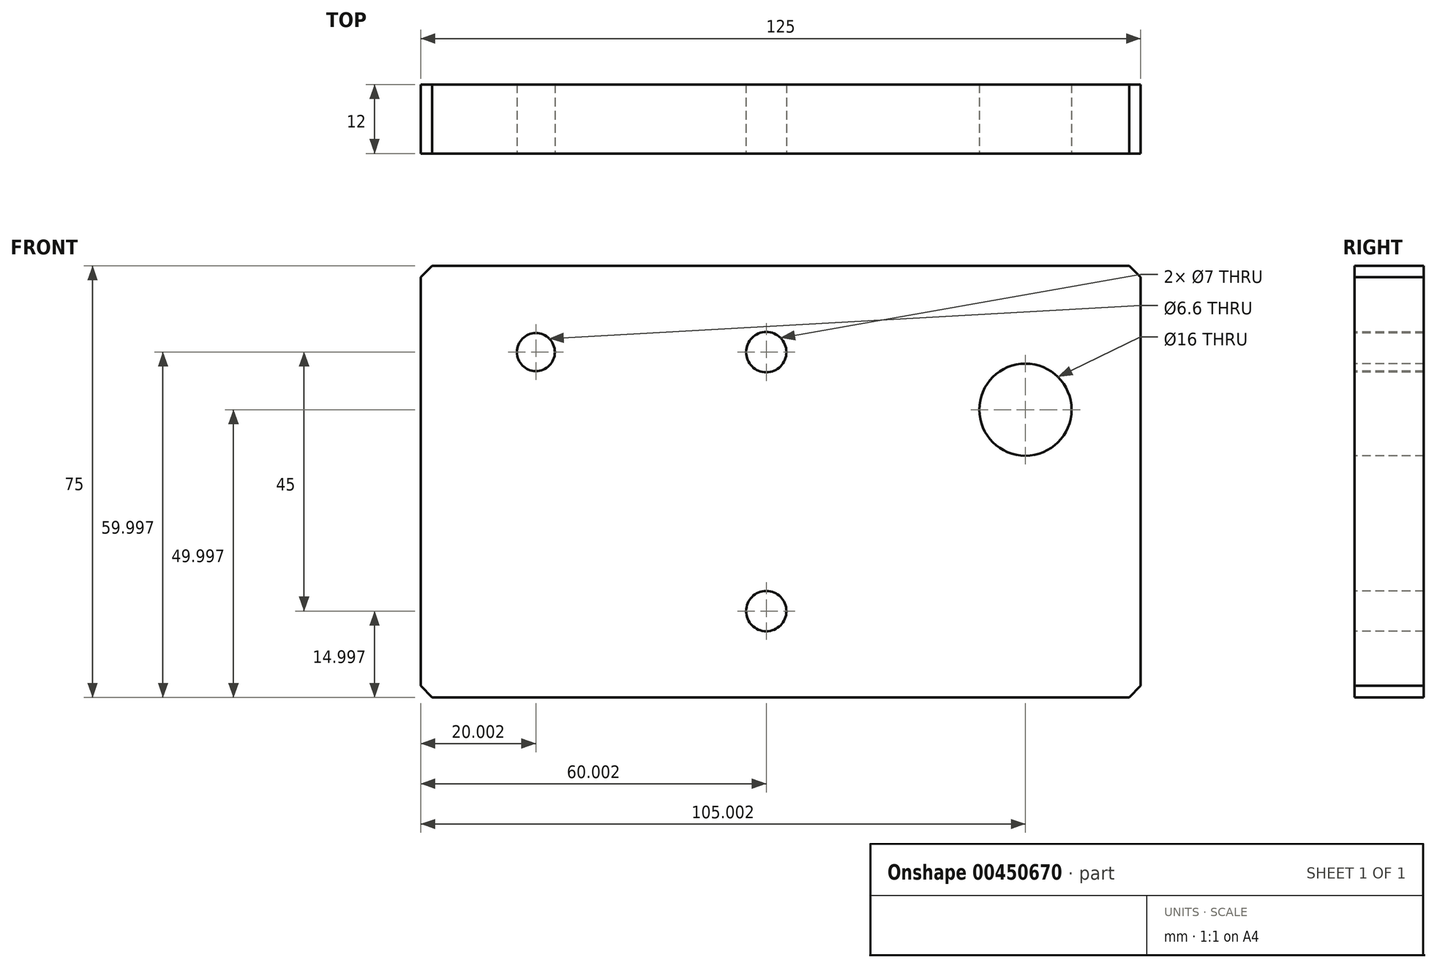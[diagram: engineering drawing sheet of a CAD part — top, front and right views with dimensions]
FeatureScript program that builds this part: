
annotation { "Feature Type Name" : "Feature", "Feature Type Description" : "" }
export const myFeature = defineFeature(function(context is Context, id is Id, definition is map)
    precondition{}
    {
        {
            var Q0;
            Q0=qCreatedBy(makeId("Front.planeOp"),FACE);
            var sketch = newSketch(context, id + "F0", { "sketchPlane" : qUnion([Q0])});
            skLineSegment(sketch, "E0", {"start": v(56.37, -134.41) * mm, "end": v(44.37, -134.41) * mm});
            skLineSegment(sketch, "E1", {"start": v(56.37, -59.41) * mm, "end": v(44.37, -59.41) * mm});
            skLineSegment(sketch, "E2", {"start": v(56.37, -59.41) * mm, "end": v(56.37, -134.41) * mm});
            skLineSegment(sketch, "E3", {"start": v(44.37, -59.41) * mm, "end": v(44.37, -134.41) * mm});
            skLineSegment(sketch, "E4", {"start": v(-19.08, -134.41) * mm, "end": v(-140.08, -134.41) * mm});
            skLineSegment(sketch, "E5", {"start": v(-17.08, -132.41) * mm, "end": v(-19.08, -134.41) * mm});
            skLineSegment(sketch, "E6", {"start": v(-19.08, -59.41) * mm, "end": v(-140.08, -59.41) * mm});
            skLineSegment(sketch, "E7", {"start": v(-17.08, -61.41) * mm, "end": v(-19.08, -59.41) * mm});
            skLineSegment(sketch, "E8", {"start": v(-17.08, -61.41) * mm, "end": v(-17.08, -132.41) * mm});
            skLineSegment(sketch, "E9", {"start": v(-142.08, -61.41) * mm, "end": v(-142.08, -132.41) * mm});
            skLineSegment(sketch, "E10", {"start": v(-140.08, -59.41) * mm, "end": v(-142.08, -61.41) * mm});
            skLineSegment(sketch, "E11", {"start": v(-140.08, -134.41) * mm, "end": v(-142.08, -132.41) * mm});
            skLineSegment(sketch, "E12", {"start": v(-37.08, -74.04) * mm, "end": v(-37.08, -94.79) * mm});
            skLineSegment(sketch, "E13", {"start": v(-47.45, -84.41) * mm, "end": v(-26.7, -84.41) * mm});
            skCircle(sketch, "E14", {"center": v(-37.08, -84.41) * mm, "radius": 8 * mm});
            skCircle(sketch, "E15", {"center": v(-37.08, -84.41) * mm, "radius": 6.92 * mm});
            skCircle(sketch, "E16", {"center": v(-82.08, -74.41) * mm, "radius": 3.5 * mm});
            skLineSegment(sketch, "E17", {"start": v(-82.08, -69.86) * mm, "end": v(-82.08, -78.96) * mm});
            skLineSegment(sketch, "E18", {"start": v(-86.63, -74.41) * mm, "end": v(-77.53, -74.41) * mm});
            skLineSegment(sketch, "E19", {"start": v(-122.08, -69.86) * mm, "end": v(-122.08, -78.96) * mm});
            skLineSegment(sketch, "E20", {"start": v(-126.63, -74.41) * mm, "end": v(-117.53, -74.41) * mm});
            skCircle(sketch, "E21", {"center": v(-82.08, -119.41) * mm, "radius": 3.5 * mm});
            skLineSegment(sketch, "E22", {"start": v(-82.08, -114.86) * mm, "end": v(-82.08, -123.96) * mm});
            skLineSegment(sketch, "E23", {"start": v(-86.63, -119.41) * mm, "end": v(-77.53, -119.41) * mm});
            skCircle(sketch, "E24", {"center": v(-122.08, -74.41) * mm, "radius": 3.3 * mm});
            skSolve(sketch);
        }
        {
            var Q0;
            Q0=makeQuery(id+"F0.imprint","IMPRINT",FACE,{"disambiguationData":[TD([[makeQuery(id+"F0.imprint","IMPRINT",EDGE,{"derivedFrom":sQuery(id+"F0.wireOp",EDGE,"E4")}),-1.0]])]});
            extrude(context, id + "F1", {"entities" : qUnion([Q0]), "oppositeDirection" : true, "depth" : 12 * mm});
        }
    });
